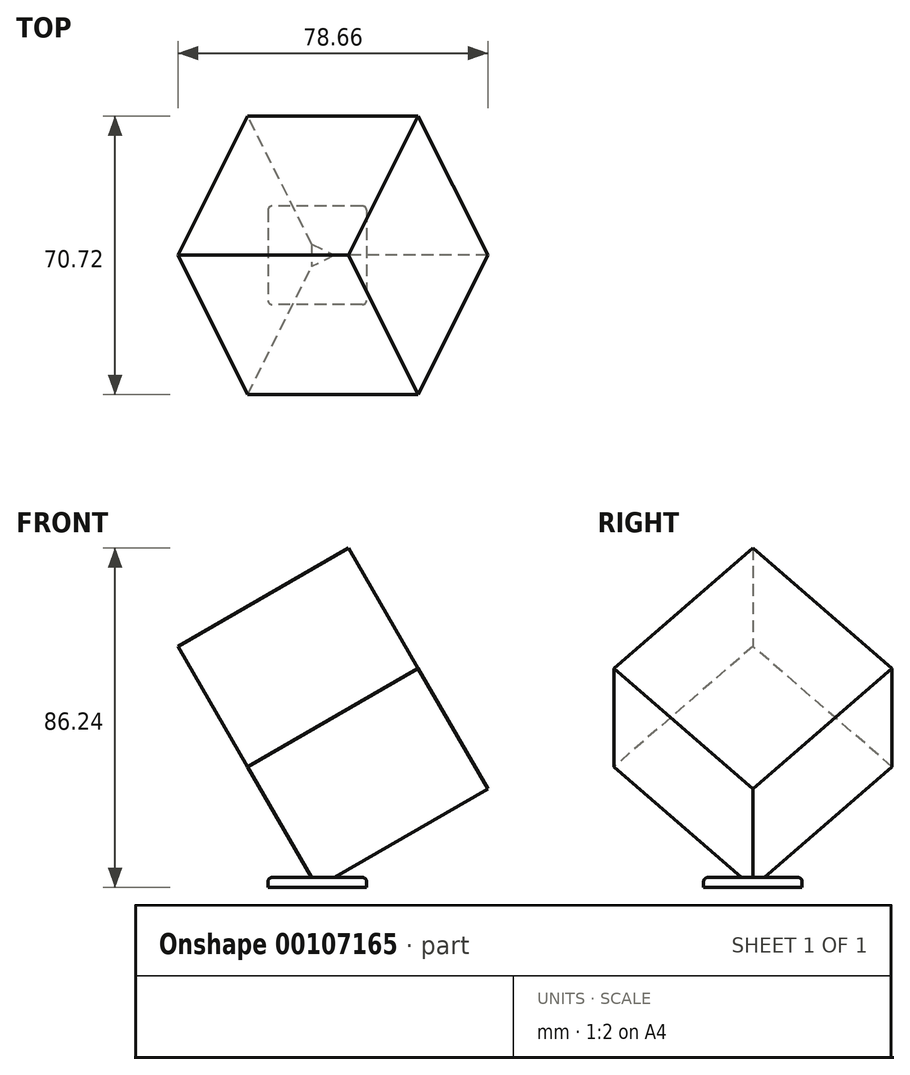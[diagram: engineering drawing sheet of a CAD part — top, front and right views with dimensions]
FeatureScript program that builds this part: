
annotation { "Feature Type Name" : "Feature", "Feature Type Description" : "" }
export const myFeature = defineFeature(function(context is Context, id is Id, definition is map)
    precondition{}
    {
        {
            var Q0;
            Q0=qCreatedBy(makeId("Top.planeOp"),FACE);
            var sketch = newSketch(context, id + "F0", { "sketchPlane" : qUnion([Q0])});
            skLineSegment(sketch, "E0.bottom", {"start": v(12.5, 12.5) * mm, "end": v(-12.5, 12.5) * mm});
            skLineSegment(sketch, "E0.top", {"start": v(12.5, -12.5) * mm, "end": v(-12.5, -12.5) * mm});
            skLineSegment(sketch, "E0.left", {"start": v(12.5, 12.5) * mm, "end": v(12.5, -12.5) * mm});
            skLineSegment(sketch, "E0.right", {"start": v(-12.5, 12.5) * mm, "end": v(-12.5, -12.5) * mm});
            skPoint(sketch, "E0.middle", {"position": v(0, 0) * mm});
            skSolve(sketch);
        }
        {
            var Q0;
            Q0 = qSketchRegion(id + "F0", true);
            extrude(context, id + "F1", {"entities" : qUnion([Q0]), "depth" : 2.5 * mm});
        }
        {
            var Q0;
            Q0=qCreatedBy(makeId("Top.planeOp"),FACE);
            var sketch = newSketch(context, id + "F2", { "sketchPlane" : qUnion([Q0])});
            skLineSegment(sketch, "E1", {"start": v(0, -12.5) * mm, "end": v(0, 12.5) * mm});
            skSolve(sketch);
        }
        {
            var Q0;
            Q0=sQuery(id+"F2.wireOp",EDGE,"E1");
            var Q1;
            Q1=qCreatedBy(makeId("Top.planeOp"),FACE);
            cPlane(context, id + "F3", {"entities" : qUnion([Q0, Q1]), "cplaneType" : CPlaneType.LINE_ANGLE, "offset" : 25 * mm, "angle" : 60 * degree, "width" : 150 * mm, "height" : 150 * mm});
        }
        {
            var Q0;
            Q0=qCreatedBy(id+"F3.planeOp",FACE);
            var sketch = newSketch(context, id + "F4", { "sketchPlane" : qUnion([Q0])});
            skLineSegment(sketch, "E2", {"start": v(0, 0) * mm, "end": v(-35.36, 35.36) * mm});
            skLineSegment(sketch, "E3", {"start": v(-35.36, 35.36) * mm, "end": v(0, 70.71) * mm});
            skLineSegment(sketch, "E4", {"start": v(0, 70.71) * mm, "end": v(35.36, 35.36) * mm});
            skLineSegment(sketch, "E5", {"start": v(35.36, 35.36) * mm, "end": v(0, 0) * mm});
            skSolve(sketch);
        }
        {
            var Q0;
            Q0 = qSketchRegion(id + "F4", true);
            extrude(context, id + "F5", {"entities" : qUnion([Q0]), "operationType" : NewBodyOperationType.ADD, "oppositeDirection" : true, "depth" : 50 * mm});
        }
        {
            var Q0;
            Q0=makeQuery(id+"F5.opExtrude","CAP_FACE",FACE,{"disambiguationData":[OSD([sQuery(id+"F4.wireOp",EDGE,"MenxZ6a5-m5ob-EJKW-wQ6i-Tr9xuhXvSayX"),sQuery(id+"F4.wireOp",EDGE,"EjZMIF6F-IWma-dYRU-pA27-k8ZBwQGSeHQS"),sQuery(id+"F4.wireOp",EDGE,"tAF2S36p-7Nr2-D8DK-khzI-aoMMl6jGgedt"),sQuery(id+"F4.wireOp",EDGE,"5pWuwPen-8ShY-Gof5-Iz1w-ntTOXJB7hcgR")])],"isStart":false});
            var Q1;
            Q1=makeQuery(id+"F5.opExtrude","SWEPT_FACE",FACE,{"disambiguationData":[OSD([sQuery(id+"F4.wireOp",EDGE,"tAF2S36p-7Nr2-D8DK-khzI-aoMMl6jGgedt")])]});
            var Q2;
            Q2=makeQuery(id+"F5.opExtrude","SWEPT_FACE",FACE,{"disambiguationData":[OSD([sQuery(id+"F4.wireOp",EDGE,"EjZMIF6F-IWma-dYRU-pA27-k8ZBwQGSeHQS")])]});
            var Q3;
            Q3=makeQuery(id+"F5.opExtrude","SWEPT_EDGE",EDGE,{"disambiguationData":[OSD([sQuery(id+"F4.wireOp",EDGE,"MenxZ6a5-m5ob-EJKW-wQ6i-Tr9xuhXvSayX"),sQuery(id+"F4.wireOp",EDGE,"5pWuwPen-8ShY-Gof5-Iz1w-ntTOXJB7hcgR")])]});
            var Q4;
            Q4=makeQuery(id+"F5.opExtrude","CAP_EDGE",EDGE,{"disambiguationData":[OSD([sQuery(id+"F4.wireOp",EDGE,"MenxZ6a5-m5ob-EJKW-wQ6i-Tr9xuhXvSayX")])],"isStart":true});
            var Q5;
            Q5=makeQuery(id+"F5.opExtrude","CAP_EDGE",EDGE,{"disambiguationData":[OSD([sQuery(id+"F4.wireOp",EDGE,"5pWuwPen-8ShY-Gof5-Iz1w-ntTOXJB7hcgR")])],"isStart":true});
            var Q6;
            Q6=makeQuery(id+"F1.opExtrude","CAP_EDGE",EDGE,{"disambiguationData":[OSD([sQuery(id+"F0.wireOp",EDGE,"E0.right")])],"isStart":false});
            var Q7;
            Q7=makeQuery(id+"F1.opExtrude","SWEPT_EDGE",EDGE,{"disambiguationData":[OSD([sQuery(id+"F0.wireOp",EDGE,"E0.top"),sQuery(id+"F0.wireOp",EDGE,"E0.right")])]});
            var Q8;
            Q8=makeQuery(id+"F1.opExtrude","CAP_EDGE",EDGE,{"disambiguationData":[OSD([sQuery(id+"F0.wireOp",EDGE,"E0.top")])],"isStart":false});
            var Q9;
            Q9=makeQuery(id+"F1.opExtrude","SWEPT_EDGE",EDGE,{"disambiguationData":[OSD([sQuery(id+"F0.wireOp",EDGE,"E0.bottom"),sQuery(id+"F0.wireOp",EDGE,"E0.right")])]});
            var Q10;
            Q10=makeQuery(id+"F1.opExtrude","CAP_EDGE",EDGE,{"disambiguationData":[OSD([sQuery(id+"F0.wireOp",EDGE,"E0.bottom")])],"isStart":false});
            var Q11;
            Q11=makeQuery(id+"F1.opExtrude","SWEPT_EDGE",EDGE,{"disambiguationData":[OSD([sQuery(id+"F0.wireOp",EDGE,"E0.bottom"),sQuery(id+"F0.wireOp",EDGE,"E0.left")])]});
            var Q12;
            Q12=makeQuery(id+"F1.opExtrude","CAP_EDGE",EDGE,{"disambiguationData":[OSD([sQuery(id+"F0.wireOp",EDGE,"E0.left")])],"isStart":false});
            var Q13;
            Q13=makeQuery(id+"F1.opExtrude","SWEPT_EDGE",EDGE,{"disambiguationData":[OSD([sQuery(id+"F0.wireOp",EDGE,"E0.top"),sQuery(id+"F0.wireOp",EDGE,"E0.left")])]});
            fillet(context, id + "F6", {"entities" : qUnion([Q0, Q1, Q2, Q3, Q4, Q5, Q6, Q7, Q8, Q9, Q10, Q11, Q12, Q13]), "radius" : 1 * mm, "tangentPropagation" : true, "allowEdgeOverflow" : false});
        }
    });
